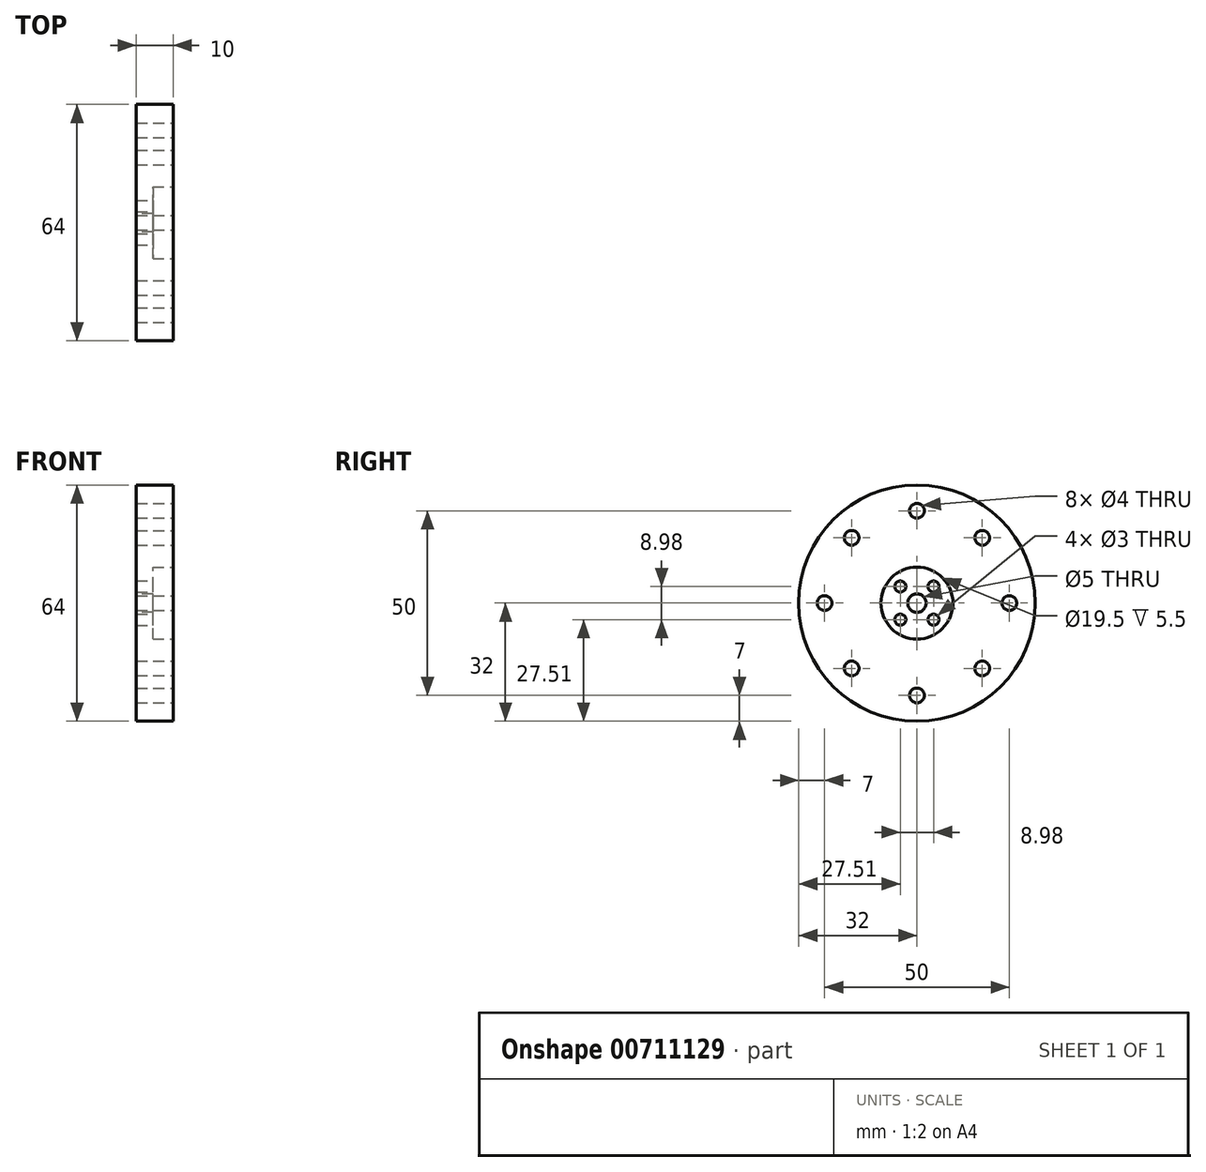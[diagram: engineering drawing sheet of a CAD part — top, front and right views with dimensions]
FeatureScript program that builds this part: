
annotation { "Feature Type Name" : "Feature", "Feature Type Description" : "" }
export const myFeature = defineFeature(function(context is Context, id is Id, definition is map)
    precondition{}
    {
        {
            var Q0;
            Q0=qCreatedBy(makeId("Right.planeOp"),FACE);
            var sketch = newSketch(context, id + "F0", { "sketchPlane" : qUnion([Q0])});
            skCircle(sketch, "E0", {"center": v(0, 0) * mm, "radius": 32 * mm});
            skCircle(sketch, "E1", {"center": v(0, 0) * mm, "radius": 2.5 * mm});
            skSolve(sketch);
        }
        {
            var Q0;
            Q0 = qSketchRegion(id + "F0", true);
            extrude(context, id + "F1", {"entities" : qUnion([Q0]), "endBound" : BoundingType.SYMMETRIC, "depth" : 10 * mm, "offsetDistance" : 25 * mm});
        }
        {
            var Q0;
            Q0=makeQuery(id+"F1.opExtrude","CAP_FACE",FACE,{"disambiguationData":[OSD([sQuery(id+"F0.wireOp",EDGE,"E0"),sQuery(id+"F0.wireOp",EDGE,"E1")])],"isStart":false});
            var sketch = newSketch(context, id + "F2", { "sketchPlane" : qUnion([Q0])});
            skCircle(sketch, "E2", {"center": v(0, 0) * mm, "radius": 9.75 * mm});
            skSolve(sketch);
        }
        {
            var Q0;
            Q0 = qSketchRegion(id + "F2", true);
            extrude(context, id + "F3", {"entities" : qUnion([Q0]), "operationType" : NewBodyOperationType.REMOVE, "oppositeDirection" : true, "depth" : 5.5 * mm, "offsetDistance" : 25 * mm});
        }
        {
            var Q0;
            Q0=makeQuery(id+"F3.boolean.opBoolean","COPY",FACE,{"derivedFrom":makeQuery(id+"F3.opExtrude","CAP_FACE",FACE,{"disambiguationData":[OSD([sQuery(id+"F2.wireOp",EDGE,"E2")])],"isStart":false})});
            var sketch = newSketch(context, id + "F4", { "sketchPlane" : qUnion([Q0])});
            skLineSegment(sketch, "E3", {"start": v(-9.75, 0) * mm, "end": v(0, 0) * mm, "construction": true});
            skLineSegment(sketch, "E4", {"start": v(0, 0) * mm, "end": v(-4.5, 4.5) * mm, "construction": true});
            skCircle(sketch, "E5", {"center": v(-4.5, 4.5) * mm, "radius": 1.5 * mm});
            skCircle(sketch, "E6.1.0", {"center": v(-4.5, -4.5) * mm, "radius": 1.5 * mm});
            skCircle(sketch, "E6.2.0", {"center": v(4.5, -4.5) * mm, "radius": 1.5 * mm});
            skCircle(sketch, "E6.3.0", {"center": v(4.5, 4.5) * mm, "radius": 1.5 * mm});
            skPoint(sketch, "E6.center", {"position": v(0, 0) * mm});
            skSolve(sketch);
        }
        {
            var Q0;
            Q0 = qSketchRegion(id + "F4", true);
            extrude(context, id + "F5", {"entities" : qUnion([Q0]), "operationType" : NewBodyOperationType.REMOVE, "endBound" : BoundingType.THROUGH_ALL, "oppositeDirection" : true, "depth" : 25 * mm, "offsetDistance" : 25 * mm});
        }
        {
            var Q0;
            Q0=makeQuery(id+"F1.opExtrude","CAP_FACE",FACE,{"disambiguationData":[OSD([sQuery(id+"F0.wireOp",EDGE,"E0"),sQuery(id+"F0.wireOp",EDGE,"E1")])],"isStart":false});
            var sketch = newSketch(context, id + "F6", { "sketchPlane" : qUnion([Q0])});
            skLineSegment(sketch, "E7", {"start": v(-32, 0) * mm, "end": v(0, 0) * mm, "construction": true});
            skLineSegment(sketch, "E8", {"start": v(0, 0) * mm, "end": v(0, 32) * mm, "construction": true});
            skCircle(sketch, "E9", {"center": v(0, 25) * mm, "radius": 2 * mm});
            skCircle(sketch, "E10.1.0", {"center": v(-17.68, 17.68) * mm, "radius": 2 * mm});
            skCircle(sketch, "E10.2.0", {"center": v(-25, 0) * mm, "radius": 2 * mm});
            skCircle(sketch, "E10.3.0", {"center": v(-17.68, -17.68) * mm, "radius": 2 * mm});
            skCircle(sketch, "E10.4.0", {"center": v(0, -25) * mm, "radius": 2 * mm});
            skCircle(sketch, "E10.5.0", {"center": v(17.68, -17.68) * mm, "radius": 2 * mm});
            skCircle(sketch, "E10.6.0", {"center": v(25, 0) * mm, "radius": 2 * mm});
            skCircle(sketch, "E10.7.0", {"center": v(17.68, 17.68) * mm, "radius": 2 * mm});
            skPoint(sketch, "E10.center", {"position": v(0, 0) * mm});
            skSolve(sketch);
        }
        {
            var Q0;
            Q0 = qSketchRegion(id + "F6", true);
            extrude(context, id + "F7", {"entities" : qUnion([Q0]), "operationType" : NewBodyOperationType.REMOVE, "endBound" : BoundingType.THROUGH_ALL, "oppositeDirection" : true, "depth" : 25 * mm, "offsetDistance" : 25 * mm});
        }
    });
